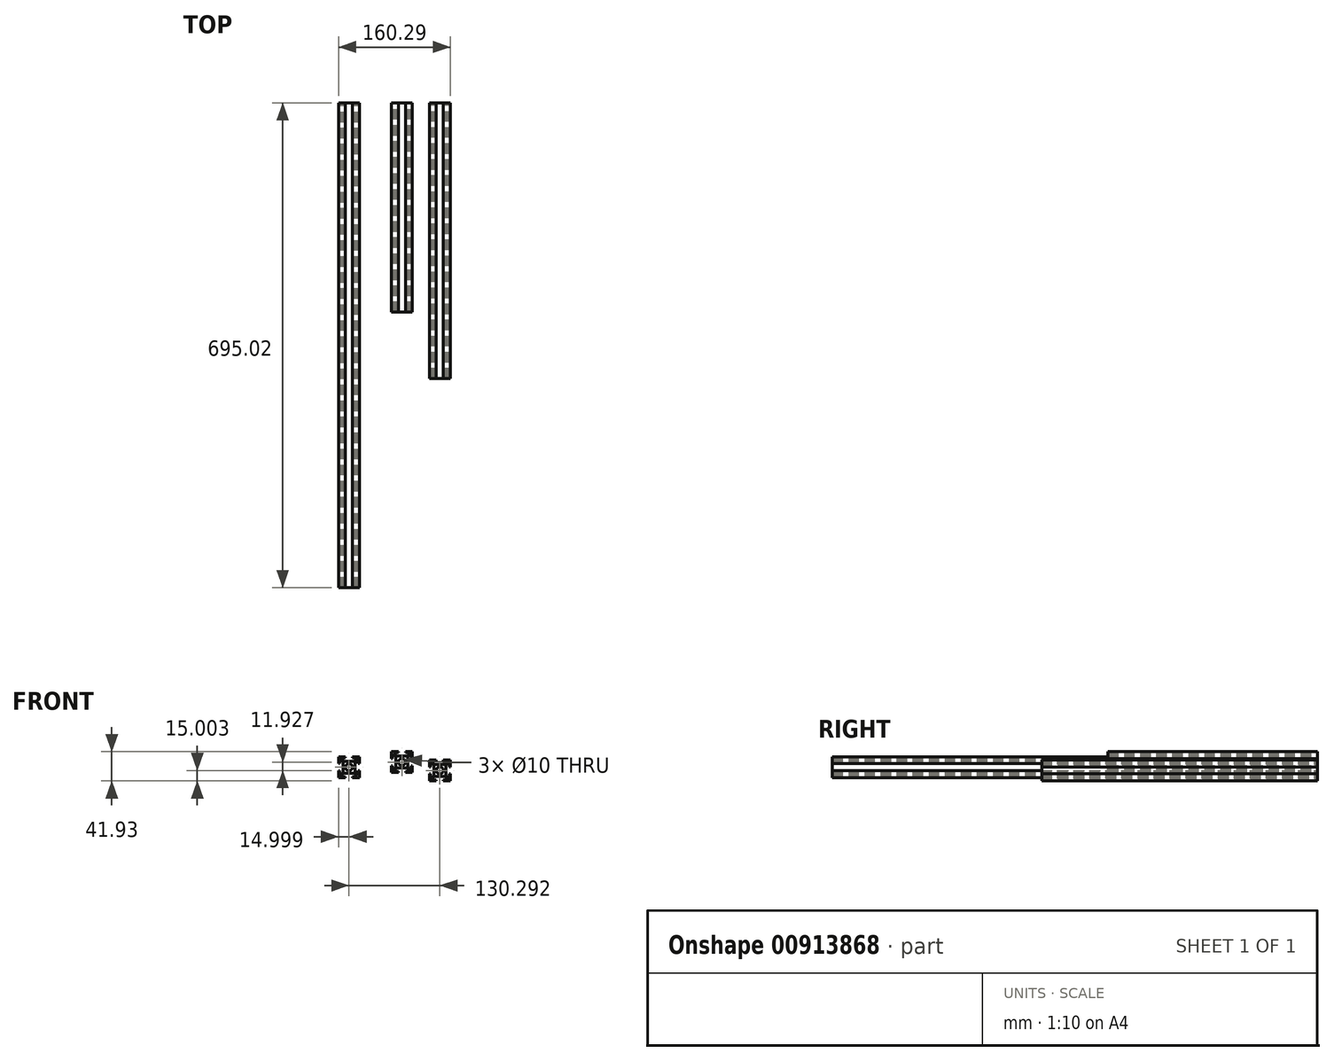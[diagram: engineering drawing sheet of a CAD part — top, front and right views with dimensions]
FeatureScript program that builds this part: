
annotation { "Feature Type Name" : "Feature", "Feature Type Description" : "" }
export const myFeature = defineFeature(function(context is Context, id is Id, definition is map)
    precondition{}
    {
        {
            var Q0;
            Q0=qCreatedBy(makeId("Front.planeOp"),FACE);
            var sketch = newSketch(context, id + "F0", { "sketchPlane" : qUnion([Q0])});
            skLineSegment(sketch, "E0", {"start": v(0, -15) * mm, "end": v(0, 15) * mm, "construction": true});
            skLineSegment(sketch, "E1", {"start": v(15, 0) * mm, "end": v(-15, 0) * mm, "construction": true});
            skLineSegment(sketch, "E2", {"start": v(0, 8.5) * mm, "end": v(7.35, 8.5) * mm});
            skLineSegment(sketch, "E3", {"start": v(7.35, 8.5) * mm, "end": v(10.18, 11.33) * mm});
            skLineSegment(sketch, "E4", {"start": v(10.18, 11.33) * mm, "end": v(10.18, 13.5) * mm});
            skLineSegment(sketch, "E5", {"start": v(10.18, 13.5) * mm, "end": v(5, 13.5) * mm});
            skLineSegment(sketch, "E6", {"start": v(5, 13.5) * mm, "end": v(5, 15) * mm});
            skLineSegment(sketch, "E7", {"start": v(5, 15) * mm, "end": v(15, 15) * mm});
            skLineSegment(sketch, "E8", {"start": v(0, 0) * mm, "end": v(15, 15) * mm, "construction": true});
            skLineSegment(sketch, "E9.MirrorCS", {"start": v(15, 5) * mm, "end": v(15, 15) * mm});
            skLineSegment(sketch, "E10.MirrorCS", {"start": v(13.5, 5) * mm, "end": v(15, 5) * mm});
            skLineSegment(sketch, "E11.MirrorCS", {"start": v(13.5, 10.18) * mm, "end": v(13.5, 5) * mm});
            skLineSegment(sketch, "E12.MirrorCS", {"start": v(11.33, 10.18) * mm, "end": v(13.5, 10.18) * mm});
            skLineSegment(sketch, "E13.MirrorCS", {"start": v(8.5, 7.35) * mm, "end": v(11.33, 10.18) * mm});
            skLineSegment(sketch, "E14.MirrorCS", {"start": v(8.5, 0) * mm, "end": v(8.5, 7.35) * mm});
            skLineSegment(sketch, "E15.MirrorCS", {"start": v(0, -8.5) * mm, "end": v(7.35, -8.5) * mm});
            skLineSegment(sketch, "E16.MirrorCS", {"start": v(8.5, 0) * mm, "end": v(8.5, -7.35) * mm});
            skLineSegment(sketch, "E17.MirrorCS", {"start": v(8.5, -7.35) * mm, "end": v(11.33, -10.18) * mm});
            skLineSegment(sketch, "E18.MirrorCS", {"start": v(7.35, -8.5) * mm, "end": v(10.18, -11.33) * mm});
            skLineSegment(sketch, "E19.MirrorCS", {"start": v(10.18, -11.33) * mm, "end": v(10.18, -13.5) * mm});
            skLineSegment(sketch, "E20.MirrorCS", {"start": v(10.18, -13.5) * mm, "end": v(5, -13.5) * mm});
            skLineSegment(sketch, "E21.MirrorCS", {"start": v(5, -13.5) * mm, "end": v(5, -15) * mm});
            skLineSegment(sketch, "E22.MirrorCS", {"start": v(5, -15) * mm, "end": v(15, -15) * mm});
            skLineSegment(sketch, "E23.MirrorCS", {"start": v(13.5, -5) * mm, "end": v(15, -5) * mm});
            skLineSegment(sketch, "E24.MirrorCS", {"start": v(13.5, -10.18) * mm, "end": v(13.5, -5) * mm});
            skLineSegment(sketch, "E25.MirrorCS", {"start": v(11.33, -10.18) * mm, "end": v(13.5, -10.18) * mm});
            skLineSegment(sketch, "E26.MirrorCS", {"start": v(0, 8.5) * mm, "end": v(-7.35, 8.5) * mm});
            skLineSegment(sketch, "E27.MirrorCS", {"start": v(-7.35, 8.5) * mm, "end": v(-10.18, 11.33) * mm});
            skLineSegment(sketch, "E28.MirrorCS", {"start": v(-10.18, 11.33) * mm, "end": v(-10.18, 13.5) * mm});
            skLineSegment(sketch, "E29.MirrorCS", {"start": v(-10.18, 13.5) * mm, "end": v(-5, 13.5) * mm});
            skLineSegment(sketch, "E30.MirrorCS", {"start": v(-5, 13.5) * mm, "end": v(-5, 15) * mm});
            skLineSegment(sketch, "E31.MirrorCS", {"start": v(-5, 15) * mm, "end": v(-15, 15) * mm});
            skLineSegment(sketch, "E32.MirrorCS", {"start": v(-13.5, 5) * mm, "end": v(-15, 5) * mm});
            skLineSegment(sketch, "E33.MirrorCS", {"start": v(-13.5, 10.18) * mm, "end": v(-13.5, 5) * mm});
            skLineSegment(sketch, "E34.MirrorCS", {"start": v(-11.33, 10.18) * mm, "end": v(-13.5, 10.18) * mm});
            skLineSegment(sketch, "E35.MirrorCS", {"start": v(-8.5, 7.35) * mm, "end": v(-11.33, 10.18) * mm});
            skLineSegment(sketch, "E36.MirrorCS", {"start": v(-8.5, 0) * mm, "end": v(-8.5, 7.35) * mm});
            skLineSegment(sketch, "E37.MirrorCS", {"start": v(-8.5, 0) * mm, "end": v(-8.5, -7.35) * mm});
            skLineSegment(sketch, "E38.MirrorCS", {"start": v(-8.5, -7.35) * mm, "end": v(-11.33, -10.18) * mm});
            skLineSegment(sketch, "E39.MirrorCS", {"start": v(-11.33, -10.18) * mm, "end": v(-13.5, -10.18) * mm});
            skLineSegment(sketch, "E40.MirrorCS", {"start": v(-13.5, -10.18) * mm, "end": v(-13.5, -5) * mm});
            skLineSegment(sketch, "E41.MirrorCS", {"start": v(-13.5, -5) * mm, "end": v(-15, -5) * mm});
            skLineSegment(sketch, "E42.MirrorCS", {"start": v(-5, -15) * mm, "end": v(-15, -15) * mm});
            skLineSegment(sketch, "E43.MirrorCS", {"start": v(-5, -13.5) * mm, "end": v(-5, -15) * mm});
            skLineSegment(sketch, "E44.MirrorCS", {"start": v(-10.18, -13.5) * mm, "end": v(-5, -13.5) * mm});
            skLineSegment(sketch, "E45.MirrorCS", {"start": v(-10.18, -11.33) * mm, "end": v(-10.18, -13.5) * mm});
            skLineSegment(sketch, "E46.MirrorCS", {"start": v(-7.35, -8.5) * mm, "end": v(-10.18, -11.33) * mm});
            skLineSegment(sketch, "E47", {"start": v(-15, 5) * mm, "end": v(-15, 15) * mm});
            skLineSegment(sketch, "E48", {"start": v(-15, -15) * mm, "end": v(-15, -5) * mm});
            skLineSegment(sketch, "E49", {"start": v(15, -15) * mm, "end": v(15, -5) * mm});
            skLineSegment(sketch, "E50", {"start": v(-7.35, -8.5) * mm, "end": v(0, -8.5) * mm});
            skCircle(sketch, "E51", {"center": v(0, 0) * mm, "radius": 5 * mm});
            skSolve(sketch);
        }
        {
            var Q0;
            Q0 = qSketchRegion(id + "F0", true);
            extrude(context, id + "F1", {"entities" : qUnion([Q0]), "depth" : 300 * mm, "offsetDistance" : 25 * mm});
        }
        {
            var Q0;
            Q0=qCreatedBy(makeId("Front.planeOp"),FACE);
            var sketch = newSketch(context, id + "F2", { "sketchPlane" : qUnion([Q0])});
            skLineSegment(sketch, "E52", {"start": v(-75.91, -22.35) * mm, "end": v(-75.91, 7.65) * mm, "construction": true});
            skLineSegment(sketch, "E53", {"start": v(-60.91, -7.35) * mm, "end": v(-90.91, -7.35) * mm, "construction": true});
            skLineSegment(sketch, "E54", {"start": v(-75.91, 1.15) * mm, "end": v(-68.56, 1.15) * mm});
            skLineSegment(sketch, "E55", {"start": v(-68.56, 1.15) * mm, "end": v(-65.73, 3.98) * mm});
            skLineSegment(sketch, "E56", {"start": v(-65.73, 3.98) * mm, "end": v(-65.73, 6.15) * mm});
            skLineSegment(sketch, "E57", {"start": v(-65.73, 6.15) * mm, "end": v(-70.91, 6.15) * mm});
            skLineSegment(sketch, "E58", {"start": v(-70.91, 6.15) * mm, "end": v(-70.91, 7.65) * mm});
            skLineSegment(sketch, "E59", {"start": v(-70.91, 7.65) * mm, "end": v(-60.91, 7.65) * mm});
            skLineSegment(sketch, "E60", {"start": v(-75.91, -7.35) * mm, "end": v(-60.91, 7.65) * mm, "construction": true});
            skLineSegment(sketch, "E61.MirrorCS", {"start": v(-60.91, -2.35) * mm, "end": v(-60.91, 7.65) * mm});
            skLineSegment(sketch, "E62.MirrorCS", {"start": v(-62.41, -2.35) * mm, "end": v(-60.91, -2.35) * mm});
            skLineSegment(sketch, "E63.MirrorCS", {"start": v(-62.41, 2.83) * mm, "end": v(-62.41, -2.35) * mm});
            skLineSegment(sketch, "E64.MirrorCS", {"start": v(-64.58, 2.83) * mm, "end": v(-62.41, 2.83) * mm});
            skLineSegment(sketch, "E65.MirrorCS", {"start": v(-67.41, 0) * mm, "end": v(-64.58, 2.83) * mm});
            skLineSegment(sketch, "E66.MirrorCS", {"start": v(-67.41, -7.35) * mm, "end": v(-67.41, 0) * mm});
            skLineSegment(sketch, "E67.MirrorCS", {"start": v(-75.91, -15.85) * mm, "end": v(-68.56, -15.85) * mm});
            skLineSegment(sketch, "E68.MirrorCS", {"start": v(-67.41, -7.35) * mm, "end": v(-67.41, -14.7) * mm});
            skLineSegment(sketch, "E69.MirrorCS", {"start": v(-67.41, -14.7) * mm, "end": v(-64.58, -17.53) * mm});
            skLineSegment(sketch, "E70.MirrorCS", {"start": v(-68.56, -15.85) * mm, "end": v(-65.73, -18.68) * mm});
            skLineSegment(sketch, "E71.MirrorCS", {"start": v(-65.73, -18.68) * mm, "end": v(-65.73, -20.85) * mm});
            skLineSegment(sketch, "E72.MirrorCS", {"start": v(-65.73, -20.85) * mm, "end": v(-70.91, -20.85) * mm});
            skLineSegment(sketch, "E73.MirrorCS", {"start": v(-70.91, -20.85) * mm, "end": v(-70.91, -22.35) * mm});
            skLineSegment(sketch, "E74.MirrorCS", {"start": v(-70.91, -22.35) * mm, "end": v(-60.91, -22.35) * mm});
            skLineSegment(sketch, "E75.MirrorCS", {"start": v(-62.41, -12.35) * mm, "end": v(-60.91, -12.35) * mm});
            skLineSegment(sketch, "E76.MirrorCS", {"start": v(-62.41, -17.53) * mm, "end": v(-62.41, -12.35) * mm});
            skLineSegment(sketch, "E77.MirrorCS", {"start": v(-64.58, -17.53) * mm, "end": v(-62.41, -17.53) * mm});
            skLineSegment(sketch, "E78.MirrorCS", {"start": v(-75.91, 1.15) * mm, "end": v(-83.26, 1.15) * mm});
            skLineSegment(sketch, "E79.MirrorCS", {"start": v(-83.26, 1.15) * mm, "end": v(-86.1, 3.98) * mm});
            skLineSegment(sketch, "E80.MirrorCS", {"start": v(-86.1, 3.98) * mm, "end": v(-86.1, 6.15) * mm});
            skLineSegment(sketch, "E81.MirrorCS", {"start": v(-86.1, 6.15) * mm, "end": v(-80.91, 6.15) * mm});
            skLineSegment(sketch, "E82.MirrorCS", {"start": v(-80.91, 6.15) * mm, "end": v(-80.91, 7.65) * mm});
            skLineSegment(sketch, "E83.MirrorCS", {"start": v(-80.91, 7.65) * mm, "end": v(-90.91, 7.65) * mm});
            skLineSegment(sketch, "E84.MirrorCS", {"start": v(-89.41, -2.35) * mm, "end": v(-90.91, -2.35) * mm});
            skLineSegment(sketch, "E85.MirrorCS", {"start": v(-89.41, 2.83) * mm, "end": v(-89.41, -2.35) * mm});
            skLineSegment(sketch, "E86.MirrorCS", {"start": v(-87.24, 2.83) * mm, "end": v(-89.41, 2.83) * mm});
            skLineSegment(sketch, "E87.MirrorCS", {"start": v(-84.41, 0) * mm, "end": v(-87.24, 2.83) * mm});
            skLineSegment(sketch, "E88.MirrorCS", {"start": v(-84.41, -7.35) * mm, "end": v(-84.41, 0) * mm});
            skLineSegment(sketch, "E89.MirrorCS", {"start": v(-84.41, -7.35) * mm, "end": v(-84.41, -14.7) * mm});
            skLineSegment(sketch, "E90.MirrorCS", {"start": v(-84.41, -14.7) * mm, "end": v(-87.24, -17.53) * mm});
            skLineSegment(sketch, "E91.MirrorCS", {"start": v(-87.24, -17.53) * mm, "end": v(-89.41, -17.53) * mm});
            skLineSegment(sketch, "E92.MirrorCS", {"start": v(-89.41, -17.53) * mm, "end": v(-89.41, -12.35) * mm});
            skLineSegment(sketch, "E93.MirrorCS", {"start": v(-89.41, -12.35) * mm, "end": v(-90.91, -12.35) * mm});
            skLineSegment(sketch, "E94.MirrorCS", {"start": v(-80.91, -22.35) * mm, "end": v(-90.91, -22.35) * mm});
            skLineSegment(sketch, "E95.MirrorCS", {"start": v(-80.91, -20.85) * mm, "end": v(-80.91, -22.35) * mm});
            skLineSegment(sketch, "E96.MirrorCS", {"start": v(-86.1, -20.85) * mm, "end": v(-80.91, -20.85) * mm});
            skLineSegment(sketch, "E97.MirrorCS", {"start": v(-86.1, -18.68) * mm, "end": v(-86.1, -20.85) * mm});
            skLineSegment(sketch, "E98.MirrorCS", {"start": v(-83.26, -15.85) * mm, "end": v(-86.1, -18.68) * mm});
            skLineSegment(sketch, "E99", {"start": v(-90.91, -2.35) * mm, "end": v(-90.91, 7.65) * mm});
            skLineSegment(sketch, "E100", {"start": v(-90.91, -22.35) * mm, "end": v(-90.91, -12.35) * mm});
            skLineSegment(sketch, "E101", {"start": v(-60.91, -22.35) * mm, "end": v(-60.91, -12.35) * mm});
            skLineSegment(sketch, "E102", {"start": v(-83.26, -15.85) * mm, "end": v(-75.91, -15.85) * mm});
            skCircle(sketch, "E103", {"center": v(-75.91, -7.35) * mm, "radius": 5 * mm});
            skSolve(sketch);
        }
        {
            var Q0;
            Q0 = qSketchRegion(id + "F2", true);
            extrude(context, id + "F3", {"entities" : qUnion([Q0]), "depth" : 695.02 * mm, "offsetDistance" : 25 * mm});
        }
        {
            var Q0;
            Q0=qCreatedBy(makeId("Front.planeOp"),FACE);
            var sketch = newSketch(context, id + "F4", { "sketchPlane" : qUnion([Q0])});
            skLineSegment(sketch, "E104", {"start": v(54.38, -26.93) * mm, "end": v(54.38, 3.07) * mm, "construction": true});
            skLineSegment(sketch, "E105", {"start": v(69.38, -11.93) * mm, "end": v(39.38, -11.93) * mm, "construction": true});
            skLineSegment(sketch, "E106", {"start": v(54.38, -3.43) * mm, "end": v(61.74, -3.43) * mm});
            skLineSegment(sketch, "E107", {"start": v(61.74, -3.43) * mm, "end": v(64.56, -0.6) * mm});
            skLineSegment(sketch, "E108", {"start": v(64.56, -0.6) * mm, "end": v(64.56, 1.57) * mm});
            skLineSegment(sketch, "E109", {"start": v(64.56, 1.57) * mm, "end": v(59.38, 1.57) * mm});
            skLineSegment(sketch, "E110", {"start": v(59.38, 1.57) * mm, "end": v(59.38, 3.07) * mm});
            skLineSegment(sketch, "E111", {"start": v(59.38, 3.07) * mm, "end": v(69.38, 3.07) * mm});
            skLineSegment(sketch, "E112", {"start": v(54.38, -11.93) * mm, "end": v(69.38, 3.07) * mm, "construction": true});
            skLineSegment(sketch, "E113.MirrorCS", {"start": v(69.38, -6.93) * mm, "end": v(69.38, 3.07) * mm});
            skLineSegment(sketch, "E114.MirrorCS", {"start": v(67.88, -6.93) * mm, "end": v(69.38, -6.93) * mm});
            skLineSegment(sketch, "E115.MirrorCS", {"start": v(67.88, -1.74) * mm, "end": v(67.88, -6.93) * mm});
            skLineSegment(sketch, "E116.MirrorCS", {"start": v(65.71, -1.74) * mm, "end": v(67.88, -1.74) * mm});
            skLineSegment(sketch, "E117.MirrorCS", {"start": v(62.88, -4.57) * mm, "end": v(65.71, -1.74) * mm});
            skLineSegment(sketch, "E118.MirrorCS", {"start": v(62.88, -11.93) * mm, "end": v(62.88, -4.57) * mm});
            skLineSegment(sketch, "E119.MirrorCS", {"start": v(54.38, -20.43) * mm, "end": v(61.74, -20.43) * mm});
            skLineSegment(sketch, "E120.MirrorCS", {"start": v(62.88, -11.93) * mm, "end": v(62.88, -19.28) * mm});
            skLineSegment(sketch, "E121.MirrorCS", {"start": v(62.88, -19.28) * mm, "end": v(65.71, -22.1) * mm});
            skLineSegment(sketch, "E122.MirrorCS", {"start": v(61.74, -20.43) * mm, "end": v(64.56, -23.26) * mm});
            skLineSegment(sketch, "E123.MirrorCS", {"start": v(64.56, -23.26) * mm, "end": v(64.56, -25.43) * mm});
            skLineSegment(sketch, "E124.MirrorCS", {"start": v(64.56, -25.43) * mm, "end": v(59.38, -25.43) * mm});
            skLineSegment(sketch, "E125.MirrorCS", {"start": v(59.38, -25.43) * mm, "end": v(59.38, -26.93) * mm});
            skLineSegment(sketch, "E126.MirrorCS", {"start": v(59.38, -26.93) * mm, "end": v(69.38, -26.93) * mm});
            skLineSegment(sketch, "E127.MirrorCS", {"start": v(67.88, -16.93) * mm, "end": v(69.38, -16.93) * mm});
            skLineSegment(sketch, "E128.MirrorCS", {"start": v(67.88, -22.1) * mm, "end": v(67.88, -16.93) * mm});
            skLineSegment(sketch, "E129.MirrorCS", {"start": v(65.71, -22.1) * mm, "end": v(67.88, -22.1) * mm});
            skLineSegment(sketch, "E130.MirrorCS", {"start": v(54.38, -3.43) * mm, "end": v(47.03, -3.43) * mm});
            skLineSegment(sketch, "E131.MirrorCS", {"start": v(47.03, -3.43) * mm, "end": v(44.2, -0.6) * mm});
            skLineSegment(sketch, "E132.MirrorCS", {"start": v(44.2, -0.6) * mm, "end": v(44.2, 1.57) * mm});
            skLineSegment(sketch, "E133.MirrorCS", {"start": v(44.2, 1.57) * mm, "end": v(49.38, 1.57) * mm});
            skLineSegment(sketch, "E134.MirrorCS", {"start": v(49.38, 1.57) * mm, "end": v(49.38, 3.07) * mm});
            skLineSegment(sketch, "E135.MirrorCS", {"start": v(49.38, 3.07) * mm, "end": v(39.38, 3.07) * mm});
            skLineSegment(sketch, "E136.MirrorCS", {"start": v(40.88, -6.93) * mm, "end": v(39.38, -6.93) * mm});
            skLineSegment(sketch, "E137.MirrorCS", {"start": v(40.88, -1.74) * mm, "end": v(40.88, -6.93) * mm});
            skLineSegment(sketch, "E138.MirrorCS", {"start": v(43.05, -1.74) * mm, "end": v(40.88, -1.74) * mm});
            skLineSegment(sketch, "E139.MirrorCS", {"start": v(45.88, -4.57) * mm, "end": v(43.05, -1.74) * mm});
            skLineSegment(sketch, "E140.MirrorCS", {"start": v(45.88, -11.93) * mm, "end": v(45.88, -4.57) * mm});
            skLineSegment(sketch, "E141.MirrorCS", {"start": v(45.88, -11.93) * mm, "end": v(45.88, -19.28) * mm});
            skLineSegment(sketch, "E142.MirrorCS", {"start": v(45.88, -19.28) * mm, "end": v(43.05, -22.1) * mm});
            skLineSegment(sketch, "E143.MirrorCS", {"start": v(43.05, -22.1) * mm, "end": v(40.88, -22.1) * mm});
            skLineSegment(sketch, "E144.MirrorCS", {"start": v(40.88, -22.1) * mm, "end": v(40.88, -16.93) * mm});
            skLineSegment(sketch, "E145.MirrorCS", {"start": v(40.88, -16.93) * mm, "end": v(39.38, -16.93) * mm});
            skLineSegment(sketch, "E146.MirrorCS", {"start": v(49.38, -26.93) * mm, "end": v(39.38, -26.93) * mm});
            skLineSegment(sketch, "E147.MirrorCS", {"start": v(49.38, -25.43) * mm, "end": v(49.38, -26.93) * mm});
            skLineSegment(sketch, "E148.MirrorCS", {"start": v(44.2, -25.43) * mm, "end": v(49.38, -25.43) * mm});
            skLineSegment(sketch, "E149.MirrorCS", {"start": v(44.2, -23.26) * mm, "end": v(44.2, -25.43) * mm});
            skLineSegment(sketch, "E150.MirrorCS", {"start": v(47.03, -20.43) * mm, "end": v(44.2, -23.26) * mm});
            skLineSegment(sketch, "E151", {"start": v(39.38, -6.93) * mm, "end": v(39.38, 3.07) * mm});
            skLineSegment(sketch, "E152", {"start": v(39.38, -26.93) * mm, "end": v(39.38, -16.93) * mm});
            skLineSegment(sketch, "E153", {"start": v(69.38, -26.93) * mm, "end": v(69.38, -16.93) * mm});
            skLineSegment(sketch, "E154", {"start": v(47.03, -20.43) * mm, "end": v(54.38, -20.43) * mm});
            skCircle(sketch, "E155", {"center": v(54.38, -11.93) * mm, "radius": 5 * mm});
            skSolve(sketch);
        }
        {
            var Q0;
            Q0=makeQuery(id+"F4.imprint","IMPRINT",FACE,{"disambiguationData":[TD([[makeQuery(id+"F4.imprint","IMPRINT",EDGE,{"derivedFrom":sQuery(id+"F4.wireOp",EDGE,"E106")}),-1.0]])]});
            var Q1;
            Q1 = qConstructionFilter(qBodyType(qCreatedBy(id + "F4" ,EDGE), BodyType.WIRE), ConstructionObject.NO);
            extrude(context, id + "F5", {"entities" : qUnion([Q0]), "surfaceEntities" : qUnion([Q1]), "depth" : 395.1 * mm, "offsetDistance" : 25 * mm});
        }
    });
